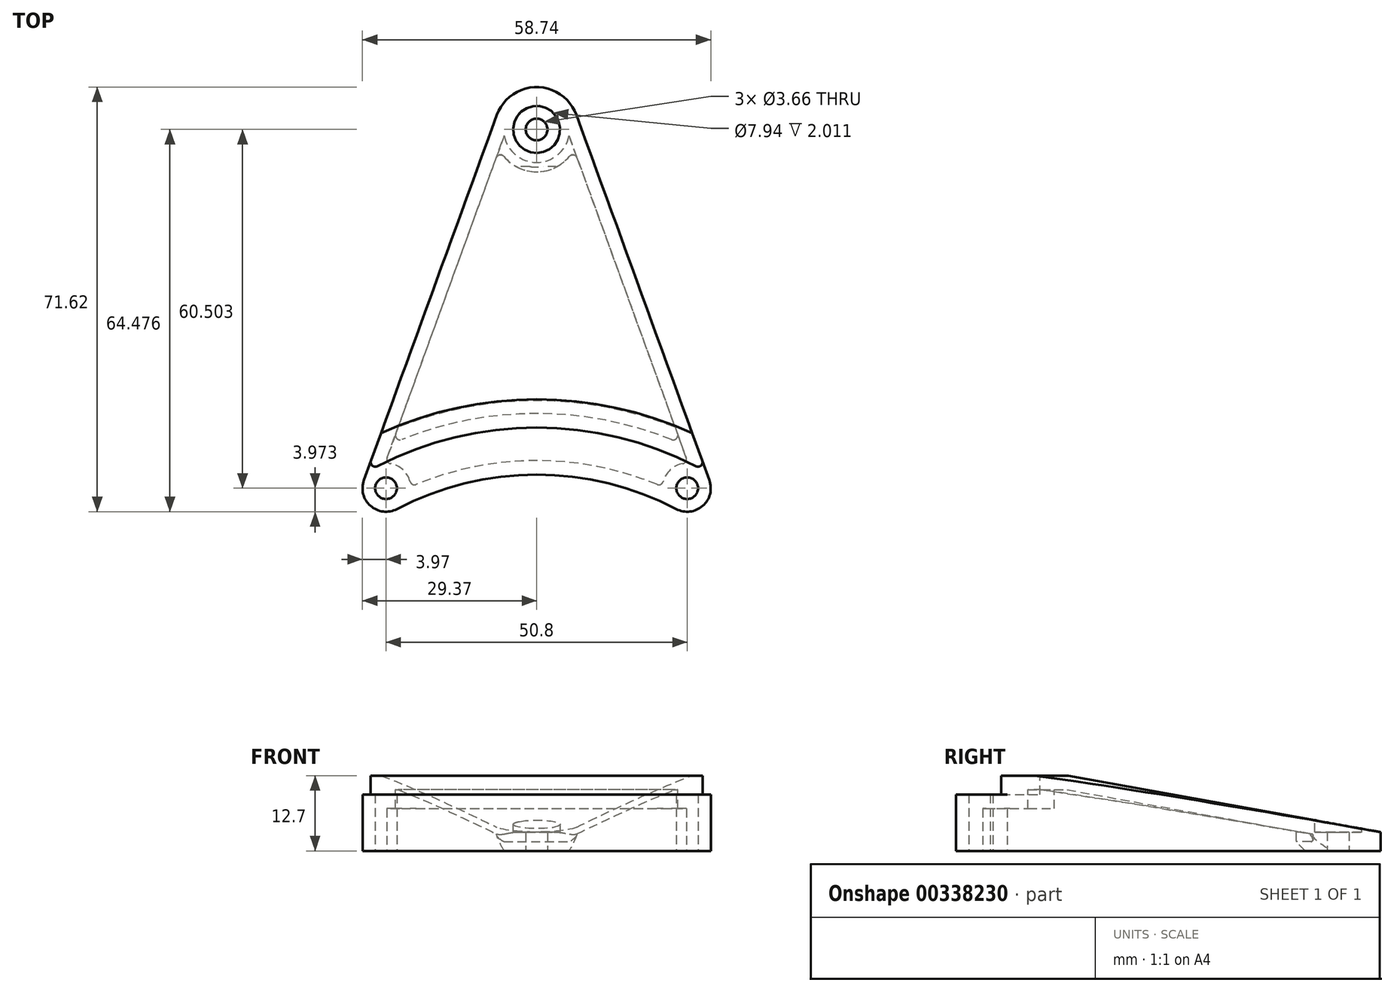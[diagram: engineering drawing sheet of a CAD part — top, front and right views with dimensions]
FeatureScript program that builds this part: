
annotation { "Feature Type Name" : "Feature", "Feature Type Description" : "" }
export const myFeature = defineFeature(function(context is Context, id is Id, definition is map)
    precondition{}
    {
        {
            var Q0;
            Q0=qCreatedBy(makeId("Top.planeOp"),FACE);
            var sketch = newSketch(context, id + "F0", { "sketchPlane" : qUnion([Q0])});
            skLineSegment(sketch, "E0", {"start": v(0, 0) * mm, "end": v(0, 50.8) * mm, "construction": true});
            skArc(sketch, "E1", {"start": v(23.56, 45) * mm, "mid": v(0, 50.8) * mm, "end": v(-23.56, 45) * mm});
            skArc(sketch, "E2", {"start": v(-29.13, 49.88) * mm, "mid": v(-28.01, 45.54) * mm, "end": v(-23.56, 45) * mm});
            skLineSegment(sketch, "E3", {"start": v(-25.4, 48.52) * mm, "end": v(0, 48.52) * mm, "construction": true});
            skLineSegment(sketch, "E4", {"start": v(0, 48.52) * mm, "end": v(25.4, 48.52) * mm, "construction": true});
            skArc(sketch, "E5", {"start": v(23.56, 45) * mm, "mid": v(28.01, 45.54) * mm, "end": v(29.13, 49.88) * mm});
            skLineSegment(sketch, "E6", {"start": v(-29.13, 49.88) * mm, "end": v(-6.71, 111.47) * mm});
            skArc(sketch, "E7", {"start": v(6.71, 111.47) * mm, "mid": v(0, 116.17) * mm, "end": v(-6.71, 111.47) * mm});
            skLineSegment(sketch, "E8", {"start": v(0, 50.8) * mm, "end": v(0, 109.03) * mm, "construction": true});
            skLineSegment(sketch, "E9", {"start": v(6.71, 111.47) * mm, "end": v(29.13, 49.88) * mm});
            skCircle(sketch, "E10", {"center": v(0, 109.03) * mm, "radius": 1.83 * mm});
            skCircle(sketch, "E11", {"center": v(25.4, 48.52) * mm, "radius": 1.83 * mm});
            skCircle(sketch, "E12", {"center": v(-25.4, 48.52) * mm, "radius": 1.83 * mm});
            skLineSegment(sketch, "E13", {"start": v(-6.71, 111.47) * mm, "end": v(-6.71, 80.67) * mm, "construction": true});
            skLineSegment(sketch, "E14", {"start": v(-6.71, 80.67) * mm, "end": v(-17.92, 80.67) * mm, "construction": true});
            skSolve(sketch);
        }
        {
            var Q0;
            Q0 = qSketchRegion(id + "F0", true);
            extrude(context, id + "F1", {"entities" : qUnion([Q0]), "depth" : 12.7 * mm});
        }
        {
            var Q0;
            Q0=qCreatedBy(makeId("Right.planeOp"),FACE);
            var sketch = newSketch(context, id + "F2", { "sketchPlane" : qUnion([Q0])});
            skLineSegment(sketch, "E15", {"start": v(63.5, 12.7) * mm, "end": v(58.74, 12.7) * mm});
            skLineSegment(sketch, "E16", {"start": v(58.74, 12.7) * mm, "end": v(58.74, 9.53) * mm});
            skLineSegment(sketch, "E17", {"start": v(58.74, 9.53) * mm, "end": v(50.8, 9.52) * mm});
            skLineSegment(sketch, "E18", {"start": v(50.8, 9.52) * mm, "end": v(50.8, 12.7) * mm});
            skLineSegment(sketch, "E19", {"start": v(50.8, 12.7) * mm, "end": v(58.74, 12.7) * mm, "construction": true});
            skLineSegment(sketch, "E20", {"start": v(63.5, 12.7) * mm, "end": v(116.17, 3.17) * mm});
            skLineSegment(sketch, "E21", {"start": v(116.17, 3.17) * mm, "end": v(116.17, 0) * mm});
            skLineSegment(sketch, "E22", {"start": v(116.17, 3.18) * mm, "end": v(116.17, 15.88) * mm});
            skLineSegment(sketch, "E23", {"start": v(116.17, 15.88) * mm, "end": v(50.8, 15.88) * mm});
            skLineSegment(sketch, "E24", {"start": v(50.8, 15.88) * mm, "end": v(50.8, 12.7) * mm});
            skSolve(sketch);
        }
        {
            var Q0;
            Q0=makeQuery(id+"F2.imprint","IMPRINT",FACE,{"disambiguationData":[TD([[makeQuery(id+"F2.imprint","IMPRINT",EDGE,{"derivedFrom":sQuery(id+"F2.wireOp",EDGE,"E15")}),-1.0]])]});
            var Q1;
            Q1=makeQuery(id+"F1.opExtrude","SWEPT_FACE",FACE,{"disambiguationData":[OSD([sQuery(id+"F0.wireOp",EDGE,"E1")])]});
            revolve(context, id + "F3", {"operationType" : NewBodyOperationType.REMOVE, "entities" : qUnion([Q0]), "axis" : qUnion([Q1]), "revolveType" : RevolveType.FULL, "oppositeDirection" : true});
        }
        {
            var Q0;
            Q0=makeQuery(id+"F1.opExtrude","CAP_FACE",FACE,{"disambiguationData":[OSD([sQuery(id+"F0.wireOp",EDGE,"E1"),sQuery(id+"F0.wireOp",EDGE,"E2"),sQuery(id+"F0.wireOp",EDGE,"E5"),sQuery(id+"F0.wireOp",EDGE,"E6"),sQuery(id+"F0.wireOp",EDGE,"E7"),sQuery(id+"F0.wireOp",EDGE,"E9"),sQuery(id+"F0.wireOp",EDGE,"E10"),sQuery(id+"F0.wireOp",EDGE,"E11"),sQuery(id+"F0.wireOp",EDGE,"E12")])],"isStart":true});
            cPlane(context, id + "F4", {"entities" : qUnion([Q0]), "cplaneType" : CPlaneType.OFFSET, "offset" : 3.17 * mm, "oppositeDirection" : true, "width" : 152.4 * mm, "height" : 152.4 * mm});
        }
        {
            var Q0;
            Q0=makeQuery(id+"F1.opExtrude","CAP_FACE",FACE,{"disambiguationData":[OSD([sQuery(id+"F0.wireOp",EDGE,"E1"),sQuery(id+"F0.wireOp",EDGE,"E2"),sQuery(id+"F0.wireOp",EDGE,"E5"),sQuery(id+"F0.wireOp",EDGE,"E6"),sQuery(id+"F0.wireOp",EDGE,"E7"),sQuery(id+"F0.wireOp",EDGE,"E9"),sQuery(id+"F0.wireOp",EDGE,"E10"),sQuery(id+"F0.wireOp",EDGE,"E11"),sQuery(id+"F0.wireOp",EDGE,"E12")])],"isStart":false});
            var sketch = newSketch(context, id + "F5", { "sketchPlane" : qUnion([Q0])});
            skCircle(sketch, "E25", {"center": v(0, 109.03) * mm, "radius": 3.97 * mm});
            skSolve(sketch);
        }
        {
            var Q0;
            Q0 = qSketchRegion(id + "F5", true);
            var Q1;
            Q1=qCreatedBy(id+"F4.planeOp",FACE);
            extrude(context, id + "F6", {"entities" : qUnion([Q0]), "operationType" : NewBodyOperationType.REMOVE, "endBound" : BoundingType.UP_TO_SURFACE, "oppositeDirection" : true, "endBoundEntityFace" : qUnion([Q1]), "depth" : 25.4 * mm});
        }
        {
            var Q0;
            Q0=makeQuery(id+"F1.opExtrude","CAP_FACE",FACE,{"disambiguationData":[OSD([sQuery(id+"F0.wireOp",EDGE,"E1"),sQuery(id+"F0.wireOp",EDGE,"E2"),sQuery(id+"F0.wireOp",EDGE,"E5"),sQuery(id+"F0.wireOp",EDGE,"E6"),sQuery(id+"F0.wireOp",EDGE,"E7"),sQuery(id+"F0.wireOp",EDGE,"E9"),sQuery(id+"F0.wireOp",EDGE,"E10"),sQuery(id+"F0.wireOp",EDGE,"E11"),sQuery(id+"F0.wireOp",EDGE,"E12")])],"isStart":true});
            shell(context, id + "F7", {"entities" : qUnion([Q0]), "thickness" : 2.38 * mm});
        }
        {
            var Q0;
            {var subQ0=sQuery(id+"F0.wireOp",EDGE,"E12");var subQ1=sQuery(id+"F0.wireOp",EDGE,"E11");var subQ2=sQuery(id+"F0.wireOp",EDGE,"E10");var subQ3=sQuery(id+"F0.wireOp",EDGE,"E9");var subQ4=sQuery(id+"F0.wireOp",EDGE,"E7");var subQ5=sQuery(id+"F0.wireOp",EDGE,"E6");var subQ6=sQuery(id+"F0.wireOp",EDGE,"E5");var subQ7=sQuery(id+"F0.wireOp",EDGE,"E2");var subQ8=sQuery(id+"F0.wireOp",EDGE,"E1");Q0=makeQuery(id+"F7.opShell","OFFSET_FACE",FACE,{"disambiguationData":[OSD([subQ8,subQ7,subQ6,subQ5,subQ4,subQ3,subQ2,subQ1,subQ0]),TDD([makeQuery(id+"F1.opExtrude","CAP_FACE",FACE,{"disambiguationData":[OSD([subQ8,subQ7,subQ6,subQ5,subQ4,subQ3,subQ2,subQ1,subQ0])],"isStart":true})])]});}
            var sketch = newSketch(context, id + "F8", { "sketchPlane" : qUnion([Q0])});
            skCircle(sketch, "E26", {"center": v(0, -109.03) * mm, "radius": 1.83 * mm});
            skCircle(sketch, "E27", {"center": v(0, -109.03) * mm, "radius": 7.14 * mm});
            skSolve(sketch);
        }
        {
            var Q0;
            Q0 = qSketchRegion(id + "F8", true);
            var Q1;
            Q1=makeQuery(id+"F6.boolean.opBoolean","COPY",FACE,{"derivedFrom":makeQuery(id+"F6.opExtrude","CAP_FACE",FACE,{"disambiguationData":[OSD([sQuery(id+"F5.wireOp",EDGE,"E25")])],"isStart":false})});
            extrude(context, id + "F9", {"entities" : qUnion([Q0]), "operationType" : NewBodyOperationType.ADD, "endBound" : BoundingType.UP_TO_SURFACE, "oppositeDirection" : true, "endBoundEntityFace" : qUnion([Q1]), "depth" : 25.4 * mm});
        }
        {
            var Q0;
            Q0=makeQuery(id+"F9.opExtrude","CAP_EDGE",EDGE,{"disambiguationData":[OSD([sQuery(id+"F8.wireOp",EDGE,"E27")])],"isStart":true});
            chamfer(context, id + "F10", {"entities" : qUnion([Q0]), "width" : 1.59 * mm, "tangentPropagation" : true});
        }
        {
            var Q0;
            Q0=makeQuery(id+"F3.boolean.opBoolean","INTERSECT",EDGE,{"derivedFrom":[makeQuery(id+"F1.opExtrude","SWEPT_FACE",FACE,{"disambiguationData":[OSD([sQuery(id+"F0.wireOp",EDGE,"E6")])]}),makeQuery(id+"F3.opRevolve","SWEPT_FACE",FACE,{"disambiguationData":[OSD([sQuery(id+"F2.wireOp",EDGE,"E16")])]})]});
            var Q1;
            Q1=makeQuery(id+"F3.boolean.opBoolean","INTERSECT",EDGE,{"derivedFrom":[makeQuery(id+"F1.opExtrude","SWEPT_FACE",FACE,{"disambiguationData":[OSD([sQuery(id+"F0.wireOp",EDGE,"E9")])]}),makeQuery(id+"F3.opRevolve","SWEPT_FACE",FACE,{"disambiguationData":[OSD([sQuery(id+"F2.wireOp",EDGE,"E16")])]})]});
            var Q2;
            Q2=makeQuery(id+"F9.boolean.opBoolean","INTERSECT",EDGE,{"derivedFrom":[makeQuery(id+"F7.opShell","OFFSET_FACE",FACE,{"disambiguationData":[OSD([sQuery(id+"F0.wireOp",EDGE,"E6")])]}),makeQuery(id+"F9.opExtrude","SWEPT_FACE",FACE,{"disambiguationData":[OSD([sQuery(id+"F8.wireOp",EDGE,"E27")])]})]});
            var Q3;
            Q3=makeQuery(id+"F9.boolean.opBoolean","INTERSECT",EDGE,{"derivedFrom":[makeQuery(id+"F7.opShell","OFFSET_FACE",FACE,{"disambiguationData":[OSD([sQuery(id+"F0.wireOp",EDGE,"E9")])]}),makeQuery(id+"F9.opExtrude","SWEPT_FACE",FACE,{"disambiguationData":[OSD([sQuery(id+"F8.wireOp",EDGE,"E27")])]})]});
            var Q4;
            Q4=makeQuery(id+"F7.opShell","OFFSET_EDGE",EDGE,{"disambiguationData":[OSD([sQuery(id+"F0.wireOp",EDGE,"E6"),sQuery(id+"F2.wireOp",EDGE,"E16")])]});
            var Q5;
            Q5=makeQuery(id+"F7.opShell","TWEAK_EDGE",EDGE,{"derivedFrom":[makeQuery(id+"F1.opExtrude","SWEPT_FACE",FACE,{"disambiguationData":[OSD([sQuery(id+"F0.wireOp",EDGE,"E6")])]}),makeQuery(id+"F1.opExtrude","SWEPT_FACE",FACE,{"disambiguationData":[OSD([sQuery(id+"F0.wireOp",EDGE,"E12")])]})]});
            var Q6;
            Q6=makeQuery(id+"F7.opShell","TWEAK_EDGE",EDGE,{"derivedFrom":[makeQuery(id+"F1.opExtrude","SWEPT_FACE",FACE,{"disambiguationData":[OSD([sQuery(id+"F0.wireOp",EDGE,"E1")])]}),makeQuery(id+"F1.opExtrude","SWEPT_FACE",FACE,{"disambiguationData":[OSD([sQuery(id+"F0.wireOp",EDGE,"E12")])]})]});
            var Q7;
            Q7=makeQuery(id+"F7.opShell","TWEAK_EDGE",EDGE,{"derivedFrom":[makeQuery(id+"F1.opExtrude","SWEPT_FACE",FACE,{"disambiguationData":[OSD([sQuery(id+"F0.wireOp",EDGE,"E1")])]}),makeQuery(id+"F1.opExtrude","SWEPT_FACE",FACE,{"disambiguationData":[OSD([sQuery(id+"F0.wireOp",EDGE,"E11")])]})]});
            var Q8;
            Q8=makeQuery(id+"F7.opShell","TWEAK_EDGE",EDGE,{"derivedFrom":[makeQuery(id+"F1.opExtrude","SWEPT_FACE",FACE,{"disambiguationData":[OSD([sQuery(id+"F0.wireOp",EDGE,"E9")])]}),makeQuery(id+"F1.opExtrude","SWEPT_FACE",FACE,{"disambiguationData":[OSD([sQuery(id+"F0.wireOp",EDGE,"E11")])]})]});
            var Q9;
            Q9=makeQuery(id+"F7.opShell","OFFSET_EDGE",EDGE,{"disambiguationData":[OSD([sQuery(id+"F0.wireOp",EDGE,"E9"),sQuery(id+"F2.wireOp",EDGE,"E16")])]});
            fillet(context, id + "F11", {"entities" : qUnion([Q0, Q1, Q2, Q3, Q4, Q5, Q6, Q7, Q8, Q9]), "radius" : 0.76 * mm, "tangentPropagation" : true, "allowEdgeOverflow" : false});
        }
    });
